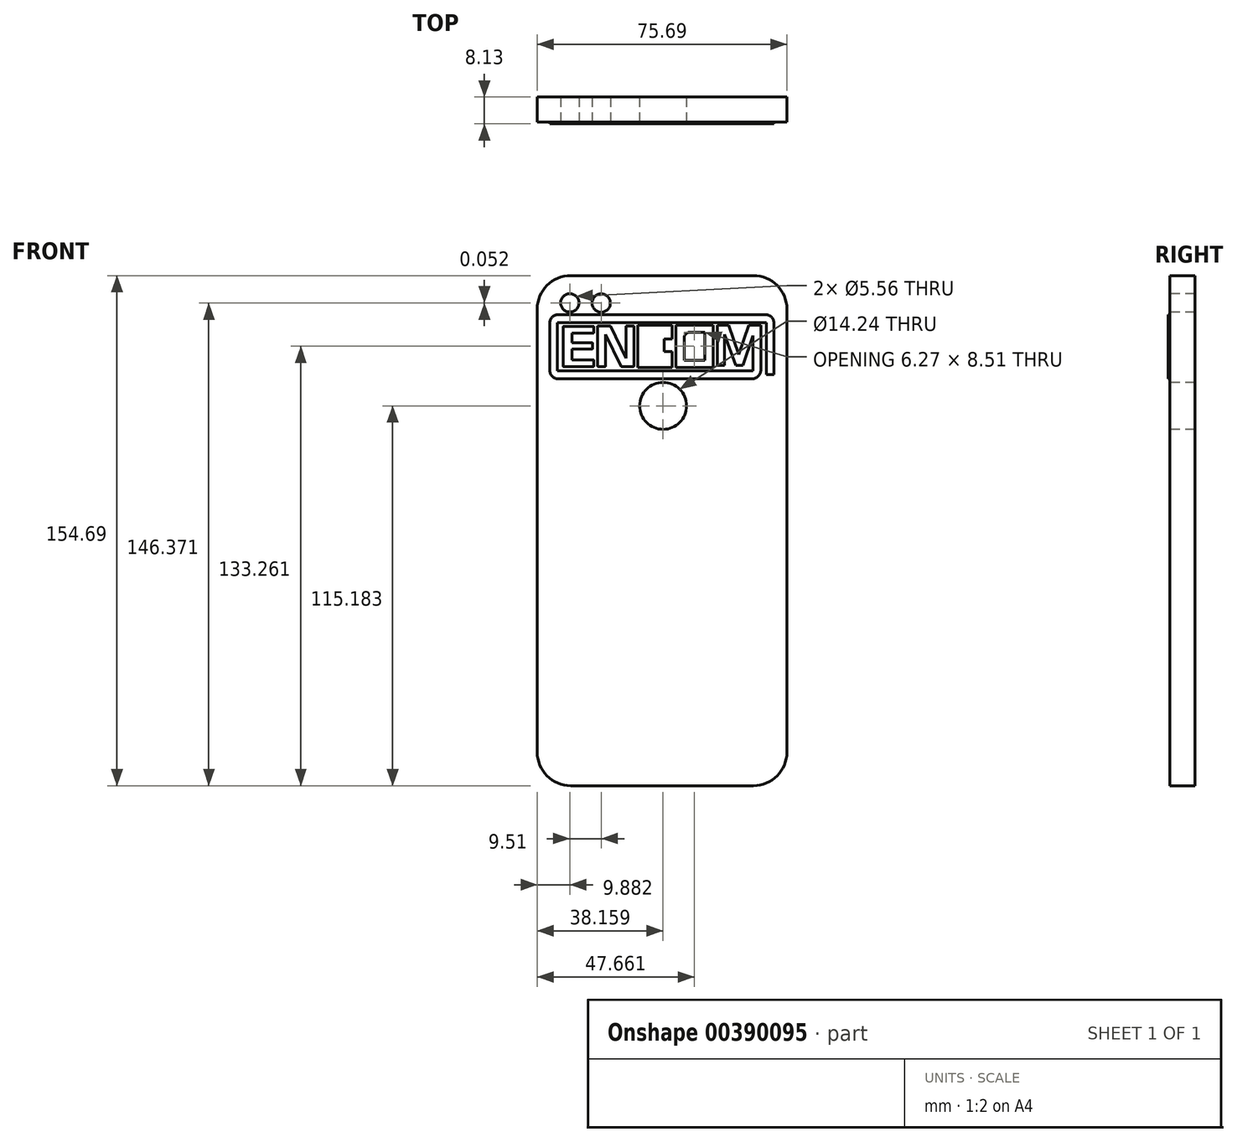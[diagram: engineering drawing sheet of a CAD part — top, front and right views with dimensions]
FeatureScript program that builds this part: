
annotation { "Feature Type Name" : "Feature", "Feature Type Description" : "" }
export const myFeature = defineFeature(function(context is Context, id is Id, definition is map)
    precondition{}
    {
        {
            var Q0;
            Q0=qCreatedBy(makeId("Front.planeOp"),FACE);
            var sketch = newSketch(context, id + "F0", { "sketchPlane" : qUnion([Q0])});
            skLineSegment(sketch, "E0.bottom", {"start": v(201.26, 129.6) * mm, "end": v(256.63, 129.6) * mm});
            skLineSegment(sketch, "E0.top", {"start": v(201.26, -25.09) * mm, "end": v(256.63, -25.09) * mm});
            skLineSegment(sketch, "E0.left", {"start": v(191.1, 119.44) * mm, "end": v(191.1, -14.93) * mm});
            skLineSegment(sketch, "E0.right", {"start": v(266.8, 119.44) * mm, "end": v(266.8, -14.93) * mm});
            skPoint(sketch, "E1.visualSharp", {"position": v(191.1, 129.6) * mm});
            skArc(sketch, "E1.filletArc", {"start": v(201.26, 129.6) * mm, "mid": v(194.08, 126.62) * mm, "end": v(191.1, 119.44) * mm});
            skPoint(sketch, "E2.visualSharp", {"position": v(266.8, 129.6) * mm});
            skArc(sketch, "E2.filletArc", {"start": v(266.8, 119.44) * mm, "mid": v(263.82, 126.62) * mm, "end": v(256.63, 129.6) * mm});
            skPoint(sketch, "E3.visualSharp", {"position": v(266.8, -25.09) * mm});
            skArc(sketch, "E3.filletArc", {"start": v(256.63, -25.09) * mm, "mid": v(263.82, -22.1) * mm, "end": v(266.8, -14.93) * mm});
            skPoint(sketch, "E4.visualSharp", {"position": v(191.1, -25.09) * mm});
            skArc(sketch, "E4.filletArc", {"start": v(191.1, -14.93) * mm, "mid": v(194.08, -22.1) * mm, "end": v(201.26, -25.09) * mm});
            skCircle(sketch, "E5", {"center": v(200.98, 121.33) * mm, "radius": 2.78 * mm});
            skCircle(sketch, "E6", {"center": v(210.5, 121.28) * mm, "radius": 2.78 * mm});
            skCircle(sketch, "E7", {"center": v(229.26, 90.1) * mm, "radius": 7.12 * mm});
            skLineSegment(sketch, "E8.bottom", {"start": v(194.83, 117.84) * mm, "end": v(263.2, 117.84) * mm});
            skLineSegment(sketch, "E8.top", {"start": v(194.83, 97.61) * mm, "end": v(263.2, 97.61) * mm});
            skLineSegment(sketch, "E8.left", {"start": v(194.83, 117.84) * mm, "end": v(194.83, 97.61) * mm});
            skLineSegment(sketch, "E8.right", {"start": v(263.2, 117.84) * mm, "end": v(263.2, 97.61) * mm});
            skSolve(sketch);
        }
        {
            var Q0;
            Q0=qCreatedBy(makeId("Front.planeOp"),FACE);
            var sketch = newSketch(context, id + "F1", { "sketchPlane" : qUnion([Q0])});
            skLineSegment(sketch, "E9.bottom", {"start": v(197.55, 117.78) * mm, "end": v(258.87, 117.78) * mm});
            skLineSegment(sketch, "E9.top", {"start": v(197.55, 98.3) * mm, "end": v(256.2, 98.3) * mm});
            skLineSegment(sketch, "E9.left", {"start": v(194.86, 115.1) * mm, "end": v(194.86, 100.98) * mm});
            skLineSegment(sketch, "E9.right", {"start": v(258.87, 117.78) * mm, "end": v(258.87, 100.98) * mm});
            skPoint(sketch, "E10.visualSharp", {"position": v(194.86, 117.78) * mm});
            skArc(sketch, "E10.filletArc", {"start": v(197.55, 117.78) * mm, "mid": v(195.65, 117) * mm, "end": v(194.86, 115.1) * mm});
            skPoint(sketch, "E11.visualSharp", {"position": v(194.86, 98.3) * mm});
            skArc(sketch, "E11.filletArc", {"start": v(194.86, 100.98) * mm, "mid": v(195.65, 99.08) * mm, "end": v(197.55, 98.3) * mm});
            skPoint(sketch, "E12.visualSharp", {"position": v(258.87, 98.3) * mm});
            skArc(sketch, "E12.filletArc", {"start": v(256.2, 98.3) * mm, "mid": v(258.09, 99.08) * mm, "end": v(258.87, 100.98) * mm});
            skLineSegment(sketch, "E13.bottom", {"start": v(199.06, 114.23) * mm, "end": v(201.62, 114.23) * mm});
            skLineSegment(sketch, "E13.top", {"start": v(199.06, 101.99) * mm, "end": v(201.62, 101.99) * mm});
            skLineSegment(sketch, "E13.left", {"start": v(198.98, 114.15) * mm, "end": v(198.98, 102.06) * mm});
            skLineSegment(sketch, "E13.right", {"start": v(201.62, 114.23) * mm, "end": v(201.62, 101.99) * mm});
            skLineSegment(sketch, "E14.bottom", {"start": v(201.62, 114.23) * mm, "end": v(208.11, 114.23) * mm});
            skLineSegment(sketch, "E14.top", {"start": v(201.62, 112.16) * mm, "end": v(208.11, 112.16) * mm});
            skLineSegment(sketch, "E14.left", {"start": v(201.62, 114.23) * mm, "end": v(201.62, 112.16) * mm});
            skLineSegment(sketch, "E14.right", {"start": v(208.19, 114.15) * mm, "end": v(208.19, 112.24) * mm});
            skLineSegment(sketch, "E15.bottom", {"start": v(201.62, 109.22) * mm, "end": v(207.84, 109.22) * mm});
            skLineSegment(sketch, "E15.top", {"start": v(201.62, 107.34) * mm, "end": v(207.84, 107.34) * mm});
            skLineSegment(sketch, "E15.left", {"start": v(201.62, 109.22) * mm, "end": v(201.62, 107.34) * mm});
            skLineSegment(sketch, "E15.right", {"start": v(207.91, 109.15) * mm, "end": v(207.91, 107.42) * mm});
            skLineSegment(sketch, "E16.bottom", {"start": v(201.62, 104.05) * mm, "end": v(208.13, 104.05) * mm});
            skLineSegment(sketch, "E16.top", {"start": v(201.62, 101.99) * mm, "end": v(208.13, 101.99) * mm});
            skLineSegment(sketch, "E16.right", {"start": v(208.2, 103.98) * mm, "end": v(208.2, 102.06) * mm});
            skLineSegment(sketch, "E17.bottom", {"start": v(209.52, 114.31) * mm, "end": v(211.8, 114.31) * mm});
            skLineSegment(sketch, "E17.top", {"start": v(209.52, 102.05) * mm, "end": v(211.72, 102.05) * mm});
            skLineSegment(sketch, "E17.left", {"start": v(209.44, 114.24) * mm, "end": v(209.44, 102.12) * mm});
            skLineSegment(sketch, "E17.right", {"start": v(211.8, 114.31) * mm, "end": v(211.8, 102.12) * mm});
            skLineSegment(sketch, "E18.bottom", {"start": v(218.12, 114.31) * mm, "end": v(220.33, 114.31) * mm});
            skLineSegment(sketch, "E18.top", {"start": v(218.05, 102.05) * mm, "end": v(220.33, 102.05) * mm});
            skLineSegment(sketch, "E18.left", {"start": v(218.05, 114.24) * mm, "end": v(218.05, 102.05) * mm});
            skLineSegment(sketch, "E18.right", {"start": v(220.4, 114.24) * mm, "end": v(220.4, 102.12) * mm});
            skLineSegment(sketch, "E19", {"start": v(218.05, 102.05) * mm, "end": v(216.61, 102.05) * mm});
            skLineSegment(sketch, "E20", {"start": v(216.54, 102.09) * mm, "end": v(211.8, 111.77) * mm});
            skLineSegment(sketch, "E21", {"start": v(218.05, 104.53) * mm, "end": v(213.28, 114.25) * mm});
            skLineSegment(sketch, "E22", {"start": v(211.8, 114.31) * mm, "end": v(213.2, 114.31) * mm});
            skLineSegment(sketch, "E23", {"start": v(213.27, 114.27) * mm, "end": v(213.28, 114.25) * mm});
            skPoint(sketch, "E24.visualSharp", {"position": v(208.19, 112.16) * mm});
            skArc(sketch, "E24.filletArc", {"start": v(208.11, 112.16) * mm, "mid": v(208.17, 112.19) * mm, "end": v(208.19, 112.24) * mm});
            skPoint(sketch, "E25.visualSharp", {"position": v(208.19, 114.23) * mm});
            skArc(sketch, "E25.filletArc", {"start": v(208.19, 114.15) * mm, "mid": v(208.17, 114.2) * mm, "end": v(208.11, 114.23) * mm});
            skPoint(sketch, "E26.visualSharp", {"position": v(198.98, 114.23) * mm});
            skArc(sketch, "E26.filletArc", {"start": v(199.06, 114.23) * mm, "mid": v(199, 114.2) * mm, "end": v(198.98, 114.15) * mm});
            skPoint(sketch, "E27.visualSharp", {"position": v(198.98, 101.99) * mm});
            skArc(sketch, "E27.filletArc", {"start": v(198.98, 102.06) * mm, "mid": v(199, 102) * mm, "end": v(199.06, 101.99) * mm});
            skPoint(sketch, "E28.visualSharp", {"position": v(208.2, 101.99) * mm});
            skArc(sketch, "E28.filletArc", {"start": v(208.13, 101.99) * mm, "mid": v(208.19, 102) * mm, "end": v(208.2, 102.06) * mm});
            skPoint(sketch, "E29.visualSharp", {"position": v(208.2, 104.05) * mm});
            skArc(sketch, "E29.filletArc", {"start": v(208.2, 103.98) * mm, "mid": v(208.19, 104.03) * mm, "end": v(208.13, 104.05) * mm});
            skPoint(sketch, "E30.visualSharp", {"position": v(207.91, 107.34) * mm});
            skArc(sketch, "E30.filletArc", {"start": v(207.84, 107.34) * mm, "mid": v(207.9, 107.36) * mm, "end": v(207.91, 107.42) * mm});
            skPoint(sketch, "E31.visualSharp", {"position": v(207.91, 109.22) * mm});
            skArc(sketch, "E31.filletArc", {"start": v(207.91, 109.15) * mm, "mid": v(207.9, 109.2) * mm, "end": v(207.84, 109.22) * mm});
            skPoint(sketch, "E32.visualSharp", {"position": v(209.44, 102.05) * mm});
            skArc(sketch, "E32.filletArc", {"start": v(209.44, 102.12) * mm, "mid": v(209.46, 102.07) * mm, "end": v(209.52, 102.05) * mm});
            skPoint(sketch, "E33.visualSharp", {"position": v(211.8, 102.05) * mm});
            skArc(sketch, "E33.filletArc", {"start": v(211.72, 102.05) * mm, "mid": v(211.78, 102.07) * mm, "end": v(211.8, 102.12) * mm});
            skPoint(sketch, "E34.visualSharp", {"position": v(209.44, 114.31) * mm});
            skArc(sketch, "E34.filletArc", {"start": v(209.52, 114.31) * mm, "mid": v(209.46, 114.3) * mm, "end": v(209.44, 114.24) * mm});
            skPoint(sketch, "E35.visualSharp", {"position": v(216.57, 102.05) * mm});
            skArc(sketch, "E35.filletArc", {"start": v(216.54, 102.09) * mm, "mid": v(216.57, 102.06) * mm, "end": v(216.61, 102.05) * mm});
            skPoint(sketch, "E36.visualSharp", {"position": v(213.25, 114.31) * mm});
            skArc(sketch, "E36.filletArc", {"start": v(213.27, 114.27) * mm, "mid": v(213.25, 114.3) * mm, "end": v(213.2, 114.31) * mm});
            skPoint(sketch, "E37.visualSharp", {"position": v(218.05, 114.31) * mm});
            skArc(sketch, "E37.filletArc", {"start": v(218.12, 114.31) * mm, "mid": v(218.07, 114.3) * mm, "end": v(218.05, 114.24) * mm});
            skPoint(sketch, "E38.visualSharp", {"position": v(220.4, 114.31) * mm});
            skArc(sketch, "E38.filletArc", {"start": v(220.4, 114.24) * mm, "mid": v(220.38, 114.3) * mm, "end": v(220.33, 114.31) * mm});
            skPoint(sketch, "E39.visualSharp", {"position": v(220.4, 102.05) * mm});
            skArc(sketch, "E39.filletArc", {"start": v(220.33, 102.05) * mm, "mid": v(220.38, 102.07) * mm, "end": v(220.4, 102.12) * mm});
            skLineSegment(sketch, "E40.bottom", {"start": v(197.24, 115.34) * mm, "end": v(256.51, 115.34) * mm});
            skLineSegment(sketch, "E40.top", {"start": v(197.24, 100.75) * mm, "end": v(256.51, 100.75) * mm});
            skLineSegment(sketch, "E40.left", {"start": v(197.24, 115.34) * mm, "end": v(197.24, 100.75) * mm});
            skLineSegment(sketch, "E40.right", {"start": v(256.51, 115.34) * mm, "end": v(256.51, 100.75) * mm});
            skLineSegment(sketch, "E41.bottom", {"start": v(256.51, 115.34) * mm, "end": v(260.54, 115.34) * mm});
            skLineSegment(sketch, "E41.top", {"start": v(256.51, 114.55) * mm, "end": v(260.54, 114.55) * mm});
            skLineSegment(sketch, "E41.left", {"start": v(256.51, 115.34) * mm, "end": v(256.51, 114.55) * mm});
            skLineSegment(sketch, "E41.right", {"start": v(260.54, 115.34) * mm, "end": v(260.54, 114.55) * mm});
            skLineSegment(sketch, "E42.bottom", {"start": v(258.87, 117.78) * mm, "end": v(260.23, 117.78) * mm});
            skLineSegment(sketch, "E42.top", {"start": v(258.87, 99.64) * mm, "end": v(262.91, 99.64) * mm});
            skLineSegment(sketch, "E42.left", {"start": v(258.87, 117.78) * mm, "end": v(258.87, 99.64) * mm});
            skLineSegment(sketch, "E42.right", {"start": v(262.91, 115.1) * mm, "end": v(262.91, 99.64) * mm});
            skLineSegment(sketch, "E43.bottom", {"start": v(262.91, 99.64) * mm, "end": v(260.54, 99.64) * mm});
            skLineSegment(sketch, "E43.top", {"start": v(262.91, 76.6) * mm, "end": v(260.54, 76.6) * mm});
            skLineSegment(sketch, "E43.left", {"start": v(262.91, 99.64) * mm, "end": v(262.91, 76.6) * mm});
            skLineSegment(sketch, "E43.right", {"start": v(260.54, 99.64) * mm, "end": v(260.54, 76.6) * mm});
            skLineSegment(sketch, "E44.bottom", {"start": v(260.54, 114.55) * mm, "end": v(258.87, 114.55) * mm});
            skLineSegment(sketch, "E44.top", {"start": v(260.54, 99.64) * mm, "end": v(258.87, 99.64) * mm});
            skLineSegment(sketch, "E44.left", {"start": v(260.54, 114.55) * mm, "end": v(260.54, 99.64) * mm});
            skLineSegment(sketch, "E44.right", {"start": v(258.87, 114.55) * mm, "end": v(258.87, 99.64) * mm});
            skLineSegment(sketch, "E45", {"start": v(256.2, 98.3) * mm, "end": v(260.54, 98.3) * mm});
            skLineSegment(sketch, "E46.bottom", {"start": v(245.69, 114.54) * mm, "end": v(247.87, 114.54) * mm});
            skLineSegment(sketch, "E46.top", {"start": v(245.69, 102.34) * mm, "end": v(247.87, 102.34) * mm});
            skLineSegment(sketch, "E46.left", {"start": v(245.69, 114.54) * mm, "end": v(245.69, 102.34) * mm});
            skLineSegment(sketch, "E46.right", {"start": v(247.87, 114.54) * mm, "end": v(247.87, 102.34) * mm});
            skLineSegment(sketch, "E47.bottom", {"start": v(237.4, 112.43) * mm, "end": v(241.9, 112.43) * mm});
            skLineSegment(sketch, "E47.top", {"start": v(235.62, 103.92) * mm, "end": v(241.9, 103.92) * mm});
            skLineSegment(sketch, "E47.left", {"start": v(235.62, 110.64) * mm, "end": v(235.62, 103.92) * mm});
            skLineSegment(sketch, "E47.right", {"start": v(241.9, 112.43) * mm, "end": v(241.9, 103.92) * mm});
            skPoint(sketch, "E48.visualSharp", {"position": v(235.62, 112.43) * mm});
            skArc(sketch, "E48.filletArc", {"start": v(237.4, 112.43) * mm, "mid": v(236.15, 111.9) * mm, "end": v(235.62, 110.64) * mm});
            skLineSegment(sketch, "E49.bottom", {"start": v(233.12, 114.62) * mm, "end": v(244.41, 114.62) * mm});
            skLineSegment(sketch, "E49.top", {"start": v(233.12, 101.73) * mm, "end": v(244.41, 101.73) * mm});
            skLineSegment(sketch, "E49.left", {"start": v(233.12, 114.62) * mm, "end": v(233.12, 101.73) * mm});
            skLineSegment(sketch, "E49.right", {"start": v(244.41, 114.62) * mm, "end": v(244.41, 101.73) * mm});
            skLineSegment(sketch, "E50.bottom", {"start": v(221.64, 114.62) * mm, "end": v(231.94, 114.62) * mm});
            skLineSegment(sketch, "E50.top", {"start": v(221.64, 101.73) * mm, "end": v(231.94, 101.73) * mm});
            skLineSegment(sketch, "E50.left", {"start": v(221.64, 114.62) * mm, "end": v(221.64, 101.73) * mm});
            skLineSegment(sketch, "E51.bottom", {"start": v(229.52, 110.35) * mm, "end": v(231.94, 110.35) * mm});
            skLineSegment(sketch, "E51.top", {"start": v(229.52, 106.6) * mm, "end": v(231.94, 106.6) * mm});
            skLineSegment(sketch, "E51.left", {"start": v(229.52, 110.35) * mm, "end": v(229.52, 106.6) * mm});
            skLineSegment(sketch, "E52", {"start": v(231.94, 114.62) * mm, "end": v(231.94, 110.35) * mm});
            skLineSegment(sketch, "E53", {"start": v(231.94, 101.73) * mm, "end": v(231.94, 106.6) * mm});
            skLineSegment(sketch, "E54", {"start": v(247.87, 114.54) * mm, "end": v(249.16, 114.54) * mm});
            skLineSegment(sketch, "E55", {"start": v(249.16, 114.54) * mm, "end": v(252.21, 105.67) * mm});
            skLineSegment(sketch, "E56", {"start": v(252.21, 105.67) * mm, "end": v(255.23, 114.54) * mm});
            skLineSegment(sketch, "E57", {"start": v(255.23, 114.54) * mm, "end": v(256.51, 114.55) * mm});
            skLineSegment(sketch, "E58", {"start": v(256.51, 111.43) * mm, "end": v(253.41, 102.34) * mm});
            skLineSegment(sketch, "E59", {"start": v(251.25, 102.34) * mm, "end": v(247.87, 111.74) * mm});
            skLineSegment(sketch, "E60", {"start": v(253.41, 102.34) * mm, "end": v(251.25, 102.34) * mm});
            skPoint(sketch, "E61.visualSharp", {"position": v(262.91, 117.78) * mm});
            skArc(sketch, "E61.filletArc", {"start": v(262.91, 115.1) * mm, "mid": v(262.12, 117) * mm, "end": v(260.23, 117.78) * mm});
            skSolve(sketch);
        }
        {
            var Q0;
            Q0 = qSketchRegion(id + "F0", true);
            var Q1;
            Q1=makeQuery(id+"F0.imprint","IMPRINT",FACE,{"disambiguationData":[TD([[makeQuery(id+"F0.imprint","IMPRINT",EDGE,{"derivedFrom":sQuery(id+"F0.wireOp",EDGE,"E8.bottom")}),-1.0]])]});
            extrude(context, id + "F2", {"entities" : qUnion([Q0, Q1]), "oppositeDirection" : true, "depth" : 7.62 * mm});
        }
        {
            var Q0;
            Q0=makeQuery(id+"F1.imprint","IMPRINT",FACE,{"disambiguationData":[TD([[makeQuery(id+"F1.imprint","IMPRINT",EDGE,{"derivedFrom":sQuery(id+"F1.wireOp",EDGE,"E13.bottom")}),-1.0]])]});
            var Q1;
            Q1=makeQuery(id+"F1.imprint","IMPRINT",FACE,{"disambiguationData":[TD([[makeQuery(id+"F1.imprint","IMPRINT",EDGE,{"derivedFrom":sQuery(id+"F1.wireOp",EDGE,"E14.bottom")}),-1.0]])]});
            var Q2;
            Q2=makeQuery(id+"F1.imprint","IMPRINT",FACE,{"disambiguationData":[TD([[makeQuery(id+"F1.imprint","IMPRINT",EDGE,{"derivedFrom":sQuery(id+"F1.wireOp",EDGE,"E15.bottom")}),-1.0]])]});
            var Q3;
            {var subQ2=sQuery(id+"F1.wireOp",EDGE,"E16.bottom");Q3=makeQuery(id+"F1.imprint","IMPRINT",FACE,{"disambiguationData":[TD([[makeQuery(id+"F1.imprint","IMPRINT",EDGE,{"derivedFrom":subQ2}),-1.0]])]});}
            var Q4;
            {var subQ1=sQuery(id+"F1.wireOp",EDGE,"E17.bottom");Q4=makeQuery(id+"F1.imprint","IMPRINT",FACE,{"disambiguationData":[TD([[makeQuery(id+"F1.imprint","IMPRINT",EDGE,{"derivedFrom":subQ1}),-1.0]])]});}
            var Q5;
            {var subQ1=sQuery(id+"F1.wireOp",EDGE,"E19");Q5=makeQuery(id+"F1.imprint","IMPRINT",FACE,{"disambiguationData":[TD([[makeQuery(id+"F1.imprint","IMPRINT",EDGE,{"derivedFrom":subQ1}),-1.0]])]});}
            var Q6;
            Q6=makeQuery(id+"F1.imprint","IMPRINT",FACE,{"disambiguationData":[TD([[makeQuery(id+"F1.imprint","IMPRINT",EDGE,{"derivedFrom":sQuery(id+"F1.wireOp",EDGE,"E18.bottom")}),-1.0]])]});
            var Q7;
            Q7=makeQuery(id+"F1.imprint","IMPRINT",FACE,{"disambiguationData":[TD([[makeQuery(id+"F1.imprint","IMPRINT",EDGE,{"derivedFrom":sQuery(id+"F1.wireOp",EDGE,"E50.bottom")}),-1.0]])]});
            var Q8;
            Q8=makeQuery(id+"F1.imprint","IMPRINT",FACE,{"disambiguationData":[TD([[makeQuery(id+"F1.imprint","IMPRINT",EDGE,{"derivedFrom":sQuery(id+"F1.wireOp",EDGE,"E47.bottom")}),1.0]])]});
            var Q9;
            {var subQ1=sQuery(id+"F1.wireOp",EDGE,"E46.bottom");Q9=makeQuery(id+"F1.imprint","IMPRINT",FACE,{"disambiguationData":[TD([[makeQuery(id+"F1.imprint","IMPRINT",EDGE,{"derivedFrom":subQ1}),-1.0]])]});}
            var Q10;
            {var subQ0=sQuery(id+"F1.wireOp",EDGE,"E54");Q10=makeQuery(id+"F1.imprint","IMPRINT",FACE,{"disambiguationData":[TD([[makeQuery(id+"F1.imprint","IMPRINT",EDGE,{"derivedFrom":subQ0}),-1.0]])]});}
            var Q11;
            {var subQ3=sQuery(id+"F1.wireOp",EDGE,"E9.bottom");Q11=makeQuery(id+"F1.imprint","IMPRINT",FACE,{"disambiguationData":[TD([[makeQuery(id+"F1.imprint","IMPRINT",EDGE,{"derivedFrom":subQ3}),-1.0]])]});}
            var Q12;
            {var subQ1=sQuery(id+"F1.wireOp",EDGE,"E41.right");Q12=makeQuery(id+"F1.imprint","IMPRINT",FACE,{"disambiguationData":[TD([[makeQuery(id+"F1.imprint","IMPRINT",EDGE,{"derivedFrom":subQ1}),1.0]])]});}
            var Q13;
            {var subQ1=sQuery(id+"F1.wireOp",EDGE,"E43.bottom");Q13=makeQuery(id+"F1.imprint","IMPRINT",FACE,{"disambiguationData":[TD([[makeQuery(id+"F1.imprint","IMPRINT",EDGE,{"derivedFrom":subQ1}),1.0]])]});}
            extrude(context, id + "F3", {"entities" : qUnion([Q0, Q1, Q2, Q3, Q4, Q5, Q6, Q7, Q8, Q9, Q10, Q11, Q12, Q13]), "depth" : 0.5 * mm});
        }
    });
